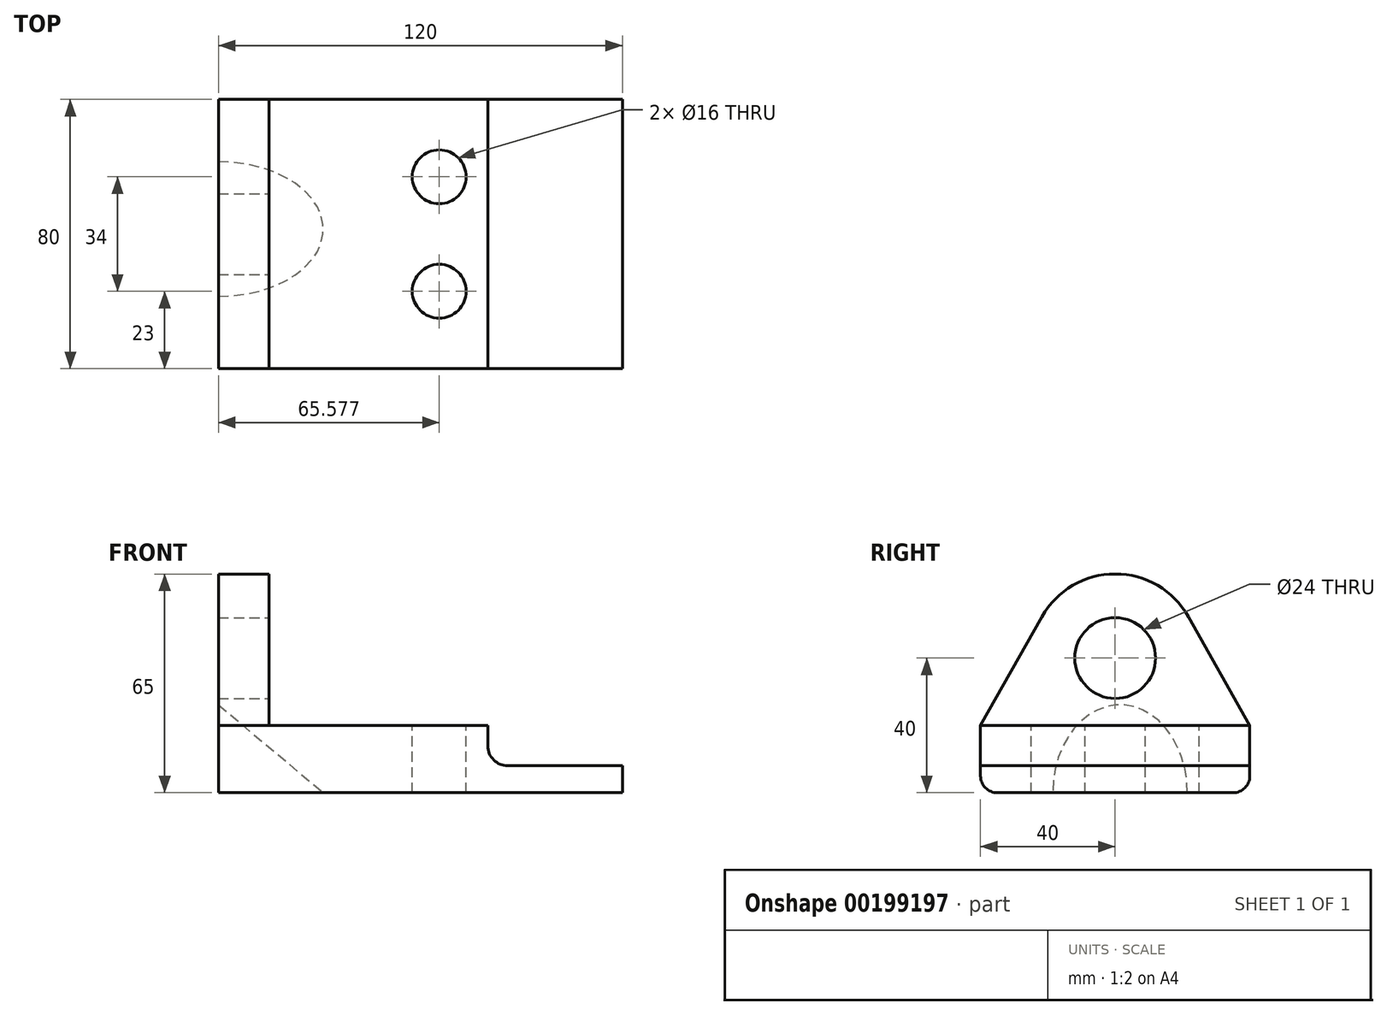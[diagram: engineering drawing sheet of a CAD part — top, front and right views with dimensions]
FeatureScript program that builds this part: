
annotation { "Feature Type Name" : "Feature", "Feature Type Description" : "" }
export const myFeature = defineFeature(function(context is Context, id is Id, definition is map)
    precondition{}
    {
        {
            var Q0;
            Q0=qCreatedBy(makeId("Front.planeOp"),FACE);
            var sketch = newSketch(context, id + "F0", { "sketchPlane" : qUnion([Q0])});
            skLineSegment(sketch, "E0", {"start": v(0, 0) * mm, "end": v(0, 65) * mm});
            skLineSegment(sketch, "E1", {"start": v(0, 65) * mm, "end": v(15, 65) * mm});
            skLineSegment(sketch, "E2", {"start": v(15, 65) * mm, "end": v(15, 20) * mm});
            skLineSegment(sketch, "E3", {"start": v(15, 20) * mm, "end": v(80, 20) * mm});
            skLineSegment(sketch, "E4", {"start": v(80, 20) * mm, "end": v(80, 8) * mm});
            skLineSegment(sketch, "E5", {"start": v(80, 8) * mm, "end": v(120, 8) * mm});
            skLineSegment(sketch, "E6", {"start": v(120, 8) * mm, "end": v(120, 0) * mm});
            skLineSegment(sketch, "E7", {"start": v(120, 0) * mm, "end": v(0, 0) * mm});
            skSolve(sketch);
        }
        {
            var Q0;
            Q0 = qSketchRegion(id + "F0", true);
            extrude(context, id + "F1", {"entities" : qUnion([Q0]), "oppositeDirection" : true, "depth" : 80 * mm});
        }
        {
            var Q0;
            Q0=makeQuery(id+"F1.opExtrude","SWEPT_FACE",FACE,{"disambiguationData":[OSD([sQuery(id+"F0.wireOp",EDGE,"E2")])]});
            var sketch = newSketch(context, id + "F2", { "sketchPlane" : qUnion([Q0])});
            skPoint(sketch, "E8.endSnap0", {"position": v(40, 20) * mm});
            skPoint(sketch, "E9.centerSnap0", {"position": v(40, 65) * mm});
            skCircle(sketch, "E10", {"center": v(40, 40) * mm, "radius": 12 * mm});
            skLineSegment(sketch, "E11", {"start": v(0, 0) * mm, "end": v(0, 20) * mm});
            skLineSegment(sketch, "E12", {"start": v(0, 20) * mm, "end": v(18.23, 52.3) * mm});
            skLineSegment(sketch, "E13", {"start": v(80, 20) * mm, "end": v(61.77, 52.3) * mm});
            skArc(sketch, "E14", {"start": v(61.77, 52.3) * mm, "mid": v(40, 65) * mm, "end": v(18.23, 52.3) * mm});
            skSolve(sketch);
        }
        {
            var Q0;
            {var subQ0=sQuery(id+"F2.wireOp",EDGE,"E12");Q0=makeQuery(id+"F2.imprint","IMPRINT",FACE,{"disambiguationData":[TD([[makeQuery(id+"F2.imprint","IMPRINT",EDGE,{"derivedFrom":subQ0}),1.0]])]});}
            var Q1;
            {var subQ0=sQuery(id+"F2.wireOp",EDGE,"E13");Q1=makeQuery(id+"F2.imprint","IMPRINT",FACE,{"disambiguationData":[TD([[makeQuery(id+"F2.imprint","IMPRINT",EDGE,{"derivedFrom":subQ0}),-1.0]])]});}
            var Q2;
            Q2=makeQuery(id+"F2.imprint","IMPRINT",FACE,{"disambiguationData":[TD([[makeQuery(id+"F2.imprint","IMPRINT",EDGE,{"derivedFrom":sQuery(id+"F2.wireOp",EDGE,"E10")}),1.0]])]});
            extrude(context, id + "F3", {"entities" : qUnion([Q0, Q1, Q2]), "operationType" : NewBodyOperationType.REMOVE, "oppositeDirection" : true, "depth" : 25 * mm});
        }
        {
            var Q0;
            Q0=makeQuery(id+"F1.opExtrude","SWEPT_EDGE",EDGE,{"disambiguationData":[OSD([sQuery(id+"F0.wireOp",EDGE,"E0"),sQuery(id+"F0.wireOp",EDGE,"E7")])]});
            cPlane(context, id + "F4", {"entities" : qUnion([Q0]), "cplaneType" : CPlaneType.LINE_ANGLE, "offset" : 25 * mm, "angle" : 50 * degree, "width" : 150 * mm, "height" : 150 * mm});
        }
        {
            var Q0;
            Q0=qCreatedBy(id+"F4.planeOp",FACE);
            var sketch = newSketch(context, id + "F5", { "sketchPlane" : qUnion([Q0])});
            skCircle(sketch, "E15", {"center": v(41.46, 0) * mm, "radius": 20 * mm});
            skSolve(sketch);
        }
        {
            var Q0;
            Q0 = qSketchRegion(id + "F5", true);
            extrude(context, id + "F6", {"entities" : qUnion([Q0]), "operationType" : NewBodyOperationType.REMOVE, "oppositeDirection" : true, "depth" : 100 * mm, "symmetric" : true});
        }
        {
            var Q0;
            Q0=makeQuery(id+"F1.opExtrude","SWEPT_EDGE",EDGE,{"disambiguationData":[OSD([sQuery(id+"F0.wireOp",EDGE,"E4"),sQuery(id+"F0.wireOp",EDGE,"E5")])]});
            fillet(context, id + "F7", {"entities" : qUnion([Q0]), "radius" : 6 * mm, "tangentPropagation" : true, "allowEdgeOverflow" : false});
        }
        {
            var Q0;
            Q0=makeQuery(id+"F1.opExtrude","CAP_EDGE",EDGE,{"disambiguationData":[OSD([sQuery(id+"F0.wireOp",EDGE,"E7")])],"isStart":true});
            var Q1;
            Q1=makeQuery(id+"F1.opExtrude","CAP_EDGE",EDGE,{"disambiguationData":[OSD([sQuery(id+"F0.wireOp",EDGE,"E7")])],"isStart":false});
            fillet(context, id + "F8", {"entities" : qUnion([Q0, Q1]), "radius" : 5 * mm, "tangentPropagation" : true, "allowEdgeOverflow" : false});
        }
        {
            var Q0;
            Q0=makeQuery(id+"F1.opExtrude","SWEPT_FACE",FACE,{"disambiguationData":[OSD([sQuery(id+"F0.wireOp",EDGE,"E3")])]});
            var sketch = newSketch(context, id + "F9", { "sketchPlane" : qUnion([Q0])});
            skCircle(sketch, "E16", {"center": v(65.58, 57) * mm, "radius": 8 * mm});
            skCircle(sketch, "E17", {"center": v(65.58, 23) * mm, "radius": 8 * mm});
            skSolve(sketch);
        }
        {
            var Q0;
            Q0 = qSketchRegion(id + "F9", true);
            extrude(context, id + "F10", {"entities" : qUnion([Q0]), "operationType" : NewBodyOperationType.REMOVE, "endBound" : BoundingType.THROUGH_ALL, "oppositeDirection" : true, "depth" : 25 * mm});
        }
    });
